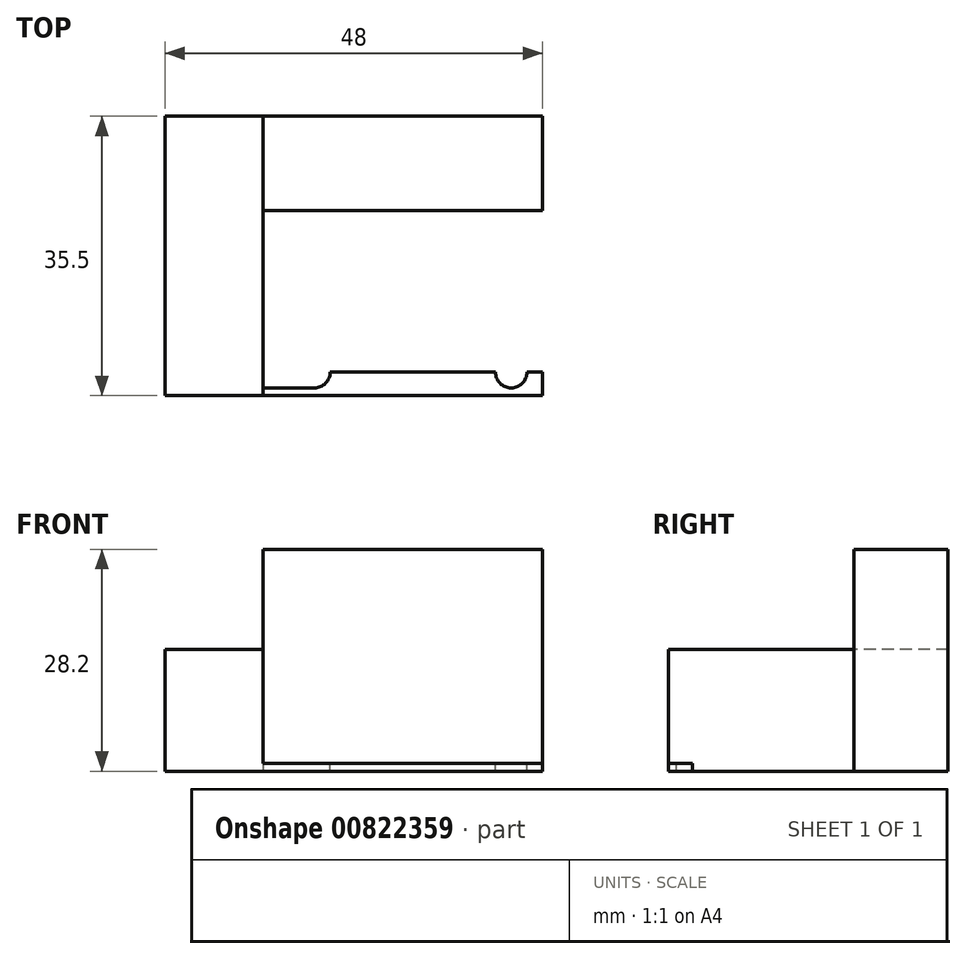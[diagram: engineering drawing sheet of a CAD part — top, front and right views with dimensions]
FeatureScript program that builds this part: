
annotation { "Feature Type Name" : "Feature", "Feature Type Description" : "" }
export const myFeature = defineFeature(function(context is Context, id is Id, definition is map)
    precondition{}
    {
        {
            var Q0;
            Q0=qCreatedBy(makeId("Top.planeOp"),FACE);
            var sketch = newSketch(context, id + "F0", { "sketchPlane" : qUnion([Q0])});
            skLineSegment(sketch, "E0.bottom", {"start": v(24, -17.75) * mm, "end": v(-24, -17.75) * mm});
            skLineSegment(sketch, "E0.top", {"start": v(24, 17.75) * mm, "end": v(-24, 17.75) * mm});
            skLineSegment(sketch, "E0.left", {"start": v(24, -17.75) * mm, "end": v(24, 17.75) * mm});
            skLineSegment(sketch, "E0.right", {"start": v(-24, -17.75) * mm, "end": v(-24, 17.75) * mm});
            skPoint(sketch, "E0.middle", {"position": v(0, 0) * mm});
            skLineSegment(sketch, "E1", {"start": v(-24, 17.75) * mm, "end": v(-11.5, 17.75) * mm});
            skLineSegment(sketch, "E2", {"start": v(-11.5, 17.75) * mm, "end": v(-11.5, -17.75) * mm});
            skLineSegment(sketch, "E3", {"start": v(-11.5, -17.75) * mm, "end": v(-24, -17.75) * mm});
            skLineSegment(sketch, "E4", {"start": v(-11.5, 17.75) * mm, "end": v(-11.5, 5.75) * mm});
            skLineSegment(sketch, "E5", {"start": v(-11.5, 5.75) * mm, "end": v(24, 5.75) * mm});
            skLineSegment(sketch, "E6", {"start": v(-11.5, -17.75) * mm, "end": v(-11.5, -16.75) * mm});
            skLineSegment(sketch, "E7", {"start": v(-11.5, -16.75) * mm, "end": v(24, -16.75) * mm});
            skLineSegment(sketch, "E8", {"start": v(24, -16.75) * mm, "end": v(24, -17.75) * mm});
            skLineSegment(sketch, "E9", {"start": v(24, -14.75) * mm, "end": v(20, -14.75) * mm});
            skLineSegment(sketch, "E10", {"start": v(20, -14.75) * mm, "end": v(-5, -14.75) * mm});
            skCircle(sketch, "E11", {"center": v(-5, -14.75) * mm, "radius": 2 * mm});
            skCircle(sketch, "E12", {"center": v(20, -14.75) * mm, "radius": 2 * mm});
            skSolve(sketch);
        }
        {
            var Q0;
            Q0=makeQuery(id+"F0.imprint","IMPRINT",FACE,{"disambiguationData":[TD([[makeQuery(id+"F0.imprint","IMPRINT",EDGE,{"derivedFrom":sQuery(id+"F0.wireOp",EDGE,"E0.right")}),-1.0]])]});
            extrude(context, id + "F1", {"entities" : qUnion([Q0]), "depth" : 14.5 * mm, "offsetDistance" : 25 * mm});
        }
        {
            var Q0;
            {var subQ0=sQuery(id+"F0.wireOp",EDGE,"E0.top");Q0=makeQuery(id+"F0.imprint","IMPRINT",FACE,{"disambiguationData":[TD([[makeQuery(id+"F0.imprint","IMPRINT",EDGE,{"derivedFrom":subQ0}),1.0]])]});}
            extrude(context, id + "F2", {"entities" : qUnion([Q0]), "operationType" : NewBodyOperationType.ADD, "depth" : 27.2 * mm, "offsetDistance" : 25 * mm});
        }
        {
            var Q0;
            {var subQ0=sQuery(id+"F0.wireOp",EDGE,"E0.top");Q0=makeQuery(id+"F0.imprint","IMPRINT",FACE,{"disambiguationData":[TD([[makeQuery(id+"F0.imprint","IMPRINT",EDGE,{"derivedFrom":subQ0}),1.0]])]});}
            var Q1;
            {var subQ0=sQuery(id+"F0.wireOp",EDGE,"E0.bottom");Q1=makeQuery(id+"F0.imprint","IMPRINT",FACE,{"disambiguationData":[TD([[makeQuery(id+"F0.imprint","IMPRINT",EDGE,{"derivedFrom":subQ0}),-1.0]])]});}
            var Q2;
            Q2=makeQuery(id+"F0.imprint","IMPRINT",FACE,{"disambiguationData":[TD([[makeQuery(id+"F0.imprint","IMPRINT",EDGE,{"derivedFrom":sQuery(id+"F0.wireOp",EDGE,"E0.right")}),-1.0]])]});
            var Q3;
            Q3=makeQuery(id+"F0.imprint","IMPRINT",FACE,{"disambiguationData":[TD([[makeQuery(id+"F0.imprint","IMPRINT",EDGE,{"derivedFrom":sQuery(id+"F0.wireOp",EDGE,"E2")}),1.0]])]});
            var Q4;
            {var subQ0=sQuery(id+"F0.wireOp",EDGE,"E11");var subQ1=sQuery(id+"F0.wireOp",EDGE,"E7");var subQ2=makeQuery(id+"F0.imprint","INTERSECT",VERTEX,{"derivedFrom":[subQ1,subQ0]});Q4=makeQuery(id+"F0.imprint","IMPRINT",FACE,{"disambiguationData":[TD([[makeQuery(id+"F0.imprint","IMPRINT",EDGE,{"disambiguationData":[TD([[subQ2,-1.0]])],"derivedFrom":subQ1}),1.0]])]});}
            var Q5;
            {var subQ1=sQuery(id+"F0.wireOp",EDGE,"E0.left");var subQ3=sQuery(id+"F0.wireOp",EDGE,"E9");var subQ4=makeQuery(id+"F0.imprint","INTERSECT",VERTEX,{"derivedFrom":[subQ1,subQ3]});Q5=makeQuery(id+"F0.imprint","IMPRINT",FACE,{"disambiguationData":[TD([[makeQuery(id+"F0.imprint","IMPRINT",EDGE,{"disambiguationData":[TD([[subQ4,-1.0]])],"derivedFrom":subQ3}),1.0]])]});}
            extrude(context, id + "F3", {"entities" : qUnion([Q0, Q1, Q2, Q3, Q4, Q5]), "operationType" : NewBodyOperationType.ADD, "oppositeDirection" : true, "depth" : 1 * mm, "offsetDistance" : 25 * mm});
        }
    });
